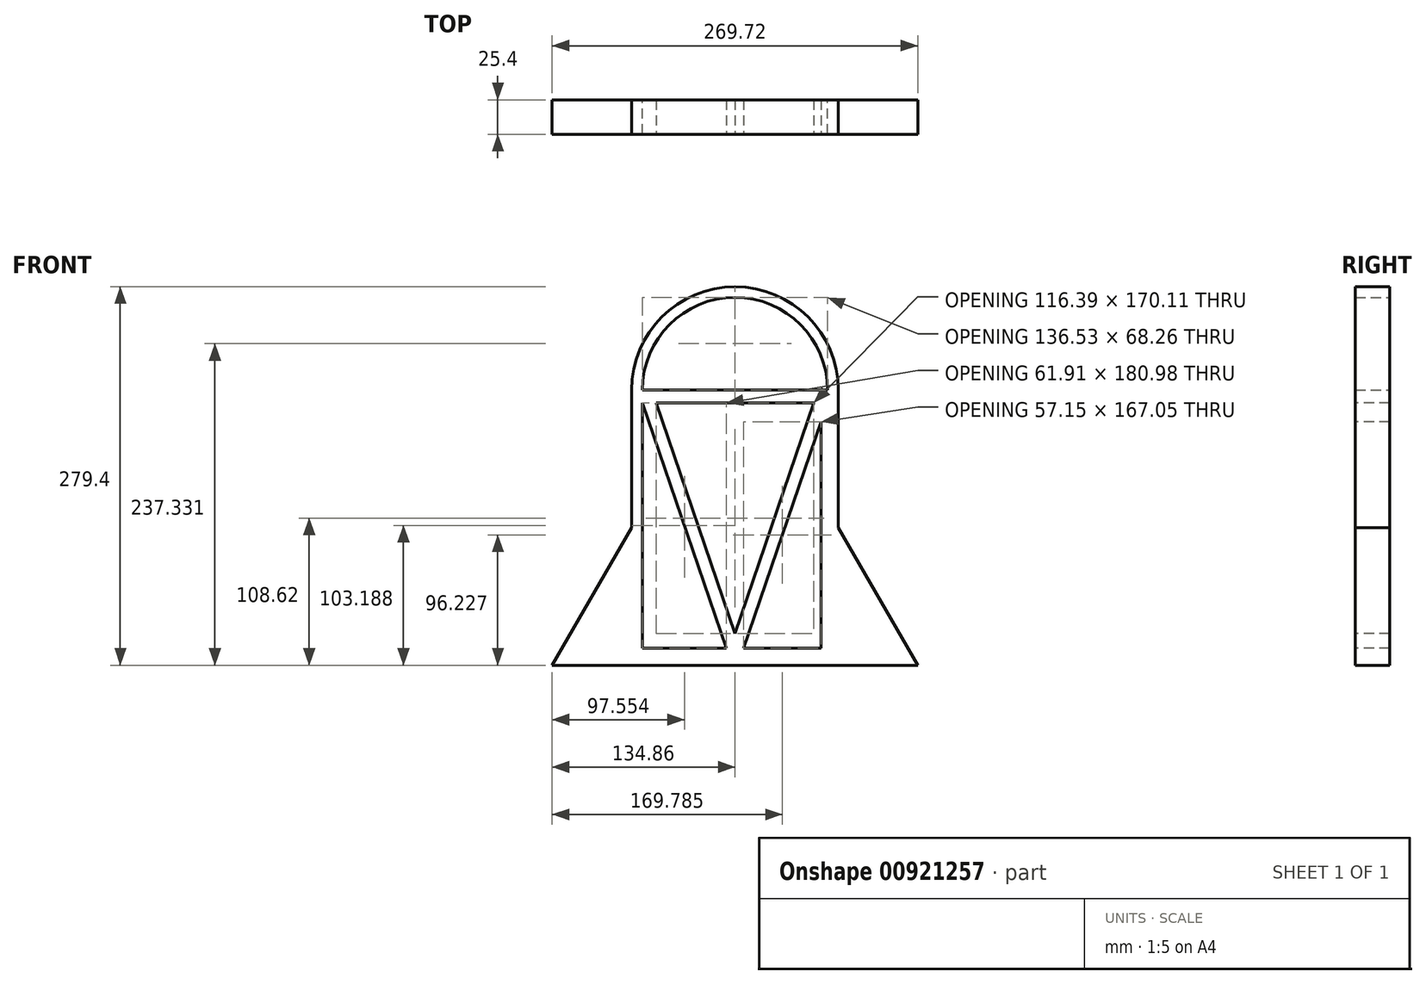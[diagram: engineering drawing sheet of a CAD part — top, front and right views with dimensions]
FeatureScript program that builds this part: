
annotation { "Feature Type Name" : "Feature", "Feature Type Description" : "" }
export const myFeature = defineFeature(function(context is Context, id is Id, definition is map)
    precondition{}
    {
        {
            var Q0;
            Q0=qCreatedBy(makeId("Front.planeOp"),FACE);
            var sketch = newSketch(context, id + "F0", { "sketchPlane" : qUnion([Q0])});
            skLineSegment(sketch, "E0.bottom", {"start": v(0, 0) * mm, "end": v(152.4, 0) * mm});
            skLineSegment(sketch, "E0.left", {"start": v(0, 0) * mm, "end": v(0, 203.2) * mm});
            skLineSegment(sketch, "E0.right", {"start": v(152.4, 0) * mm, "end": v(152.4, 203.2) * mm});
            skArc(sketch, "E1", {"start": v(152.4, 203.2) * mm, "mid": v(76.2, 279.4) * mm, "end": v(0, 203.2) * mm});
            skArc(sketch, "E2", {"start": v(144.46, 203.2) * mm, "mid": v(76.2, 271.46) * mm, "end": v(7.94, 203.2) * mm});
            skLineSegment(sketch, "E3", {"start": v(7.94, 203.2) * mm, "end": v(144.46, 203.2) * mm});
            skSolve(sketch);
        }
        {
            var Q0;
            Q0 = qSketchRegion(id + "F0", true);
            extrude(context, id + "F1", {"entities" : qUnion([Q0]), "depth" : 25.4 * mm, "offsetDistance" : 25.4 * mm});
        }
        {
            var Q0;
            Q0=makeQuery(id+"F1.opExtrude","CAP_FACE",FACE,{"disambiguationData":[OSD([sQuery(id+"F0.wireOp",EDGE,"E0.bottom"),sQuery(id+"F0.wireOp",EDGE,"E0.left"),sQuery(id+"F0.wireOp",EDGE,"E0.right"),sQuery(id+"F0.wireOp",EDGE,"E1"),sQuery(id+"F0.wireOp",EDGE,"E2"),sQuery(id+"F0.wireOp",EDGE,"E3")])],"isStart":false});
            var sketch = newSketch(context, id + "F2", { "sketchPlane" : qUnion([Q0])});
            skLineSegment(sketch, "E4", {"start": v(7.94, 12.7) * mm, "end": v(7.94, 193.68) * mm});
            skLineSegment(sketch, "E5", {"start": v(7.94, 193.68) * mm, "end": v(69.85, 12.7) * mm});
            skLineSegment(sketch, "E6", {"start": v(7.94, 12.7) * mm, "end": v(69.85, 12.7) * mm});
            skLineSegment(sketch, "E7", {"start": v(76.2, 0) * mm, "end": v(76.2, 203.2) * mm, "construction": true});
            skLineSegment(sketch, "E8.MirrorCS", {"start": v(139.7, 179.75) * mm, "end": v(82.55, 12.7) * mm});
            skLineSegment(sketch, "E9.MirrorCS", {"start": v(139.7, 12.7) * mm, "end": v(82.55, 12.7) * mm});
            skLineSegment(sketch, "E10", {"start": v(139.7, 179.75) * mm, "end": v(139.7, 12.7) * mm});
            skPoint(sketch, "E11.orphan", {"position": v(144.46, 12.7) * mm});
            skPoint(sketch, "E12.orphan", {"position": v(139.7, 193.68) * mm});
            skPoint(sketch, "E13.orphan", {"position": v(144.46, 193.68) * mm});
            skLineSegment(sketch, "E14", {"start": v(18, 193.68) * mm, "end": v(76.2, 23.56) * mm});
            skLineSegment(sketch, "E15", {"start": v(76.2, 23.56) * mm, "end": v(134.4, 193.68) * mm});
            skLineSegment(sketch, "E16", {"start": v(134.4, 193.68) * mm, "end": v(18, 193.68) * mm});
            skSolve(sketch);
        }
        {
            var Q0;
            Q0 = qSketchRegion(id + "F2", true);
            extrude(context, id + "F3", {"entities" : qUnion([Q0]), "operationType" : NewBodyOperationType.REMOVE, "endBound" : BoundingType.THROUGH_ALL, "oppositeDirection" : true, "depth" : 25.4 * mm, "offsetDistance" : 25.4 * mm});
        }
        {
            var Q0;
            Q0=makeQuery(id+"F1.opExtrude","CAP_FACE",FACE,{"disambiguationData":[OSD([sQuery(id+"F0.wireOp",EDGE,"E0.bottom"),sQuery(id+"F0.wireOp",EDGE,"E0.left"),sQuery(id+"F0.wireOp",EDGE,"E0.right"),sQuery(id+"F0.wireOp",EDGE,"E1"),sQuery(id+"F0.wireOp",EDGE,"E2"),sQuery(id+"F0.wireOp",EDGE,"E3")])],"isStart":false});
            var sketch = newSketch(context, id + "F4", { "sketchPlane" : qUnion([Q0])});
            skLineSegment(sketch, "E17", {"start": v(0, 101.6) * mm, "end": v(-58.66, 0) * mm});
            skLineSegment(sketch, "E18", {"start": v(-58.66, 0) * mm, "end": v(0, 0) * mm});
            skLineSegment(sketch, "E19", {"start": v(0, 0) * mm, "end": v(0, 101.6) * mm});
            skLineSegment(sketch, "E20", {"start": v(76.2, 193.68) * mm, "end": v(76.2, 0) * mm, "construction": true});
            skLineSegment(sketch, "E21.MirrorCS", {"start": v(152.4, 101.6) * mm, "end": v(211.06, 0) * mm});
            skLineSegment(sketch, "E22.MirrorCS", {"start": v(152.4, 0) * mm, "end": v(152.4, 101.6) * mm});
            skLineSegment(sketch, "E23.MirrorCS", {"start": v(211.06, 0) * mm, "end": v(152.4, 0) * mm});
            skSolve(sketch);
        }
        {
            var Q0;
            Q0 = qSketchRegion(id + "F4", true);
            var Q1;
            Q1=makeQuery(id+"F1.opExtrude","CAP_FACE",FACE,{"disambiguationData":[OSD([sQuery(id+"F0.wireOp",EDGE,"E0.bottom"),sQuery(id+"F0.wireOp",EDGE,"E0.left"),sQuery(id+"F0.wireOp",EDGE,"E0.right"),sQuery(id+"F0.wireOp",EDGE,"E1"),sQuery(id+"F0.wireOp",EDGE,"E2"),sQuery(id+"F0.wireOp",EDGE,"E3")])],"isStart":true});
            extrude(context, id + "F5", {"entities" : qUnion([Q0]), "operationType" : NewBodyOperationType.ADD, "endBound" : BoundingType.UP_TO_SURFACE, "oppositeDirection" : true, "depth" : 25.4 * mm, "endBoundEntityFace" : qUnion([Q1]), "offsetDistance" : 25.4 * mm});
        }
    });
